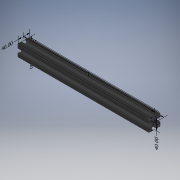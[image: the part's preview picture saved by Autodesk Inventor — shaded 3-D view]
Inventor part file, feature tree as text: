
AUTODESK INVENTOR PART (.ipt)
format: ipt  version: 2019 (Build 230136000, 136)  size: 275,456 bytes
history: native  units: mm
features: other x125, extrude x1, sketch x1
ambient origin geometry x8: Origin, YZ Plane, XZ Plane, XY Plane, X Axis, Y Axis, Z Axis, Center Point
bodies: Solid1 (feature_tree)
feature tree (127):
  other  "Annotations"
  extrude  "Extrusion1"  [1 undecoded]
  other  "CS_ANBAU_HINTEN_LINKS_XY"
  other  "CS_ANBAU_HINTEN_LINKS_YZ"
  other  "CS_ANBAU_HINTEN_LINKS_ZX"
  other  "CS_ANBAU_HINTEN_LINKS_X"
  other  "CS_ANBAU_HINTEN_LINKS_Y"
  other  "CS_ANBAU_HINTEN_LINKS_Z"
  other  "CS_ANBAU_HINTEN_LINKS_Center"
  other  "CS_ANBAU_HINTEN_OBEN_XY"
  other  "CS_ANBAU_HINTEN_OBEN_YZ"
  other  "CS_ANBAU_HINTEN_OBEN_ZX"
  other  "CS_ANBAU_HINTEN_OBEN_X"
  other  "CS_ANBAU_HINTEN_OBEN_Y"
  other  "CS_ANBAU_HINTEN_OBEN_Z"
  other  "CS_ANBAU_HINTEN_OBEN_Center"
  other  "CS_ANBAU_HINTEN_RECHTS_XY"
  other  "CS_ANBAU_HINTEN_RECHTS_YZ"
  other  "CS_ANBAU_HINTEN_RECHTS_ZX"
  other  "CS_ANBAU_HINTEN_RECHTS_X"
  other  "CS_ANBAU_HINTEN_RECHTS_Y"
  other  "CS_ANBAU_HINTEN_RECHTS_Z"
  other  "CS_ANBAU_HINTEN_RECHTS_Center"
  other  "CS_ANBAU_HINTEN_UNTEN_XY"
  other  "CS_ANBAU_HINTEN_UNTEN_YZ"
  other  "CS_ANBAU_HINTEN_UNTEN_ZX"
  other  "CS_ANBAU_HINTEN_UNTEN_X"
  other  "CS_ANBAU_HINTEN_UNTEN_Y"
  other  "CS_ANBAU_HINTEN_UNTEN_Z"
  other  "CS_ANBAU_HINTEN_UNTEN_Center"
  other  "CS_ANBAU_QUER_XY"
  other  "CS_ANBAU_QUER_YZ"
  other  "CS_ANBAU_QUER_ZX"
  other  "CS_ANBAU_QUER_X"
  other  "CS_ANBAU_QUER_Y"
  other  "CS_ANBAU_QUER_Z"
  other  "CS_ANBAU_QUER_Center"
  other  "CS_ANBAU_QUER_1_XY"
  other  "CS_ANBAU_QUER_1_YZ"
  other  "CS_ANBAU_QUER_1_ZX"
  other  "CS_ANBAU_QUER_1_X"
  other  "CS_ANBAU_QUER_1_Y"
  other  "CS_ANBAU_QUER_1_Z"
  other  "CS_ANBAU_QUER_1_Center"
  other  "CS_ANBAU_VORNE_LINKS_XY"
  other  "CS_ANBAU_VORNE_LINKS_YZ"
  other  "CS_ANBAU_VORNE_LINKS_ZX"
  other  "CS_ANBAU_VORNE_LINKS_X"
  other  "CS_ANBAU_VORNE_LINKS_Y"
  other  "CS_ANBAU_VORNE_LINKS_Z"
  other  "CS_ANBAU_VORNE_LINKS_Center"
  other  "CS_ANBAU_VORNE_OBEN_XY"
  other  "CS_ANBAU_VORNE_OBEN_YZ"
  other  "CS_ANBAU_VORNE_OBEN_ZX"
  other  "CS_ANBAU_VORNE_OBEN_X"
  other  "CS_ANBAU_VORNE_OBEN_Y"
  other  "CS_ANBAU_VORNE_OBEN_Z"
  other  "CS_ANBAU_VORNE_OBEN_Center"
  other  "CS_ANBAU_VORNE_RECHTS_XY"
  other  "CS_ANBAU_VORNE_RECHTS_YZ"
  other  "CS_ANBAU_VORNE_RECHTS_ZX"
  other  "CS_ANBAU_VORNE_RECHTS_X"
  other  "CS_ANBAU_VORNE_RECHTS_Y"
  other  "CS_ANBAU_VORNE_RECHTS_Z"
  other  "CS_ANBAU_VORNE_RECHTS_Center"
  other  "CS_ANBAU_VORNE_UNTEN_XY"
  other  "CS_ANBAU_VORNE_UNTEN_YZ"
  other  "CS_ANBAU_VORNE_UNTEN_ZX"
  other  "CS_ANBAU_VORNE_UNTEN_X"
  other  "CS_ANBAU_VORNE_UNTEN_Y"
  other  "CS_ANBAU_VORNE_UNTEN_Z"
  other  "CS_ANBAU_VORNE_UNTEN_Center"
  other  "p1_XY"
  other  "p1_YZ"
  other  "p1_ZX"
  other  "p1_X"
  other  "p1_Y"
  other  "p1_Z"
  other  "p1_Center"
  other  "p2_XY"
  other  "p2_YZ"
  other  "p2_ZX"
  other  "p2_X"
  other  "p2_Y"
  other  "p2_Z"
  other  "p2_Center"
  other  "p3_XY"
  other  "p3_YZ"
  other  "p3_ZX"
  other  "p3_X"
  other  "p3_Y"
  other  "p3_Z"
  other  "p3_Center"
  other  "p4_XY"
  other  "p4_YZ"
  other  "p4_ZX"
  other  "p4_X"
  other  "p4_Y"
  other  "p4_Z"
  other  "p4_Center"
  other  "p5_XY"
  other  "p5_YZ"
  other  "p5_ZX"
  other  "p5_X"
  other  "p5_Y"
  other  "p5_Z"
  other  "p5_Center"
  other  "pm1_XY"
  other  "pm1_YZ"
  other  "pm1_ZX"
  other  "pm1_X"
  other  "pm1_Y"
  other  "pm1_Z"
  other  "pm1_Center"
  other  "pm2_XY"
  other  "pm2_YZ"
  other  "pm2_ZX"
  other  "pm2_X"
  other  "pm2_Y"
  other  "pm2_Z"
  other  "pm2_Center"
  sketch  "Skizze_1"  dims[d0=450.0mm d1=0.0mm d2=0.0mm d3=0.0mm d4=0.0mm d5=0.0mm d6=0.0mm d10=450.0mm d11=450.0mm d7=40.0mm d8=40.0mm d9=40.0mm]
  other  "Linear Dimension 1"
  other  "Linear Dimension 2"
  other  "Linear Dimension 3"
  other  "Linear Dimension 4"
  other  "Linear Dimension 5"
note: 1 required parameter value undecoded (feature->parameter linkage not recoverable at this tier; creation-order binding heuristic only, values carry confidence <= 0.55)
